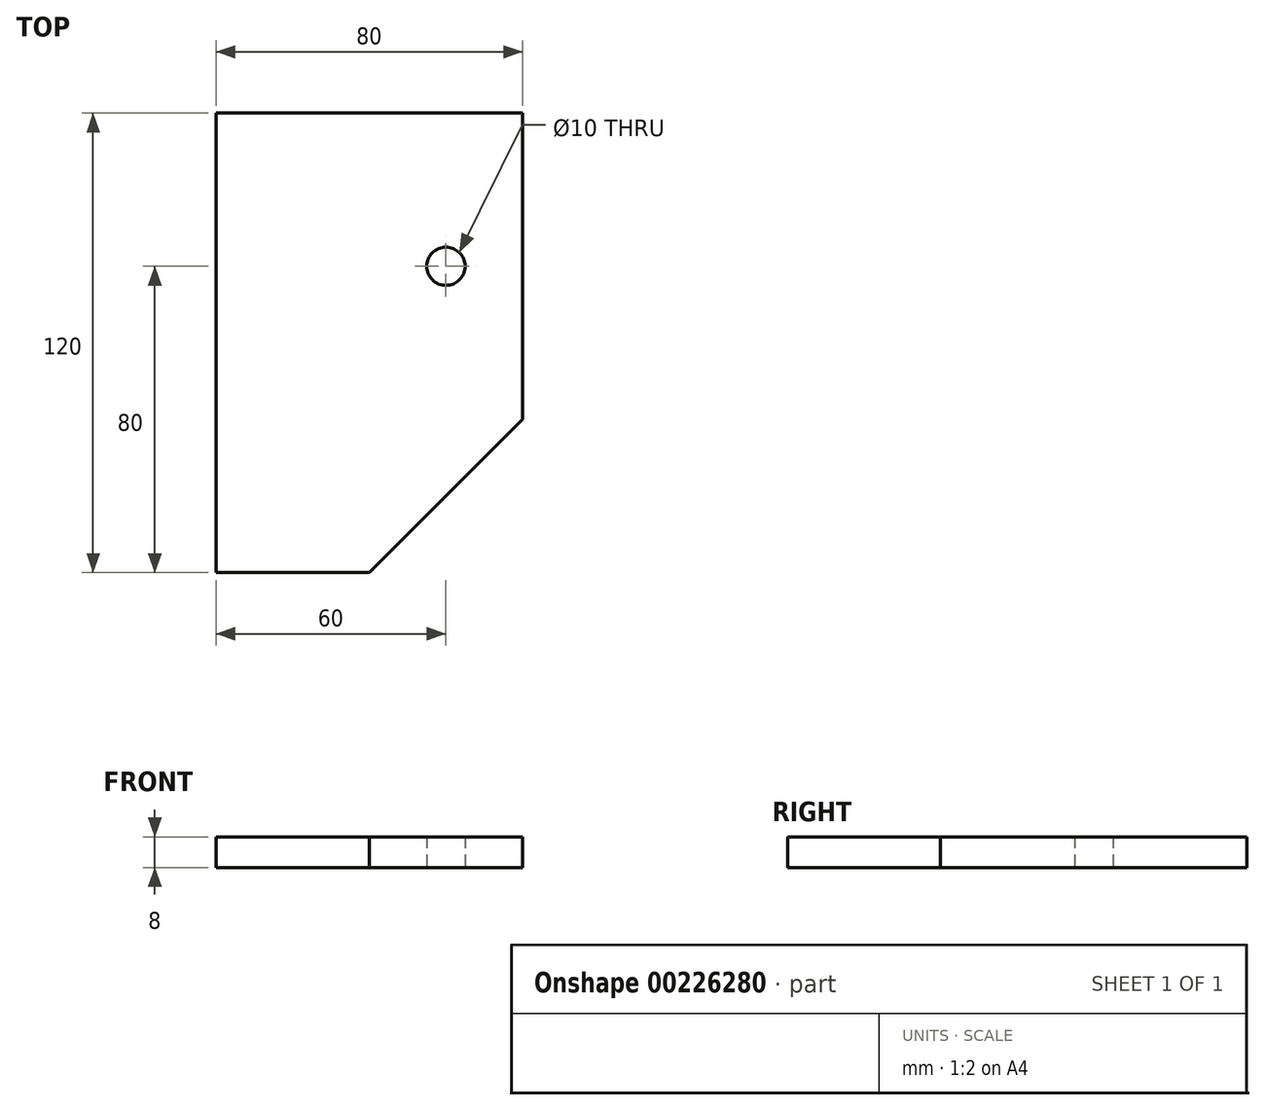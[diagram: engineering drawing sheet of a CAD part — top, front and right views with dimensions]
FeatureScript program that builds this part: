
annotation { "Feature Type Name" : "Feature", "Feature Type Description" : "" }
export const myFeature = defineFeature(function(context is Context, id is Id, definition is map)
    precondition{}
    {
        {
            var Q0;
            Q0=qCreatedBy(makeId("Top.planeOp"),FACE);
            var sketch = newSketch(context, id + "F0", { "sketchPlane" : qUnion([Q0])});
            skLineSegment(sketch, "E0.bottom", {"start": v(40, 60) * mm, "end": v(-40, 60) * mm});
            skLineSegment(sketch, "E0.top", {"start": v(0, -60) * mm, "end": v(-40, -60) * mm});
            skLineSegment(sketch, "E0.left", {"start": v(40, 60) * mm, "end": v(40, -20) * mm});
            skLineSegment(sketch, "E0.right", {"start": v(-40, 60) * mm, "end": v(-40, -60) * mm});
            skPoint(sketch, "E0.middle", {"position": v(0, 0) * mm});
            skPoint(sketch, "E1", {"position": v(40, -20) * mm});
            skLineSegment(sketch, "E2", {"start": v(40, -20) * mm, "end": v(0, -60) * mm});
            skLineSegment(sketch, "E3.right", {"start": v(40, 20) * mm, "end": v(40, -20) * mm});
            skCircle(sketch, "E4", {"center": v(20, 20) * mm, "radius": 5 * mm});
            skSolve(sketch);
        }
        {
            var Q0;
            Q0=makeQuery(id+"F0.imprint","IMPRINT",FACE,{"disambiguationData":[TD([[makeQuery(id+"F0.imprint","IMPRINT",EDGE,{"derivedFrom":sQuery(id+"F0.wireOp",EDGE,"E3.bottom")}),-1.0]])]});
            var Q1;
            Q1=makeQuery(id+"F0.imprint","IMPRINT",FACE,{"disambiguationData":[TD([[makeQuery(id+"F0.imprint","IMPRINT",EDGE,{"derivedFrom":sQuery(id+"F0.wireOp",EDGE,"E0.bottom")}),1.0]])]});
            extrude(context, id + "F1", {"entities" : qUnion([Q0, Q1]), "depth" : 8 * mm});
        }
    });
